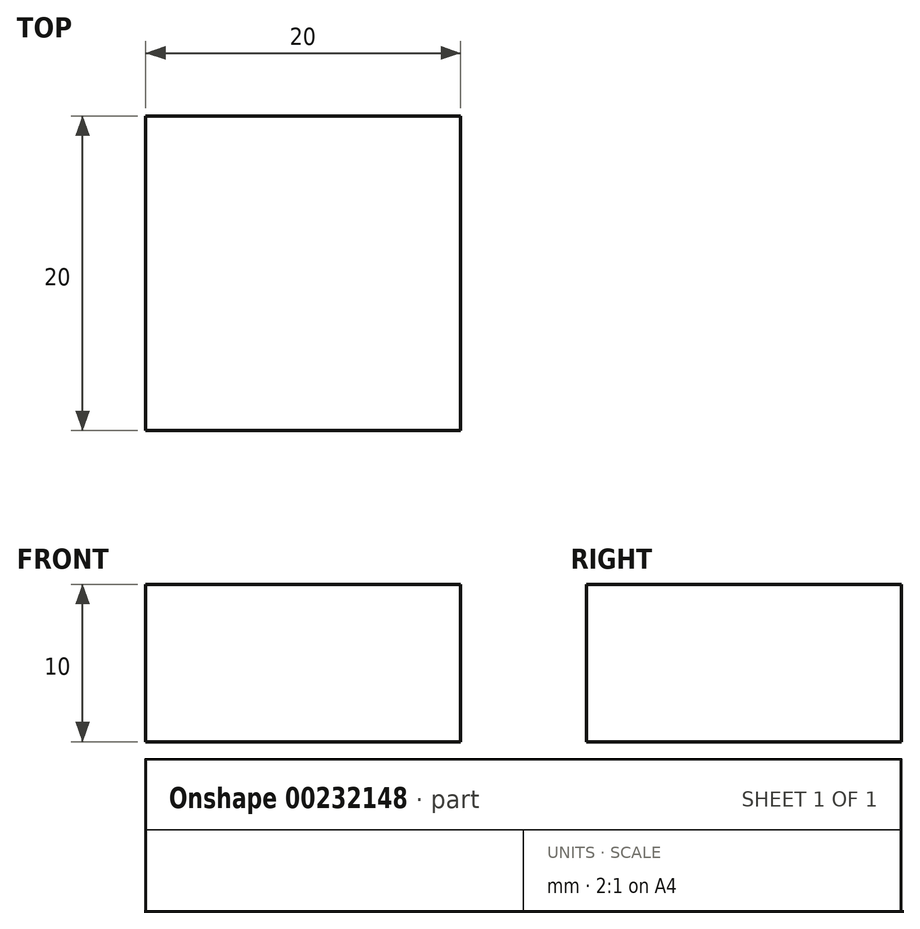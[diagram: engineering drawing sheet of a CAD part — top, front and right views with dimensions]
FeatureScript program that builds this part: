
annotation { "Feature Type Name" : "Feature", "Feature Type Description" : "" }
export const myFeature = defineFeature(function(context is Context, id is Id, definition is map)
    precondition{}
    {
        {
            var Q0;
            Q0=qCreatedBy(makeId("Top.planeOp"),FACE);
            var sketch = newSketch(context, id + "F0", { "sketchPlane" : qUnion([Q0])});
            skLineSegment(sketch, "E0.bottom", {"start": v(-10, 10) * mm, "end": v(10, 10) * mm});
            skLineSegment(sketch, "E0.top", {"start": v(-10, -10) * mm, "end": v(10, -10) * mm});
            skLineSegment(sketch, "E0.left", {"start": v(-10, 10) * mm, "end": v(-10, -10) * mm});
            skLineSegment(sketch, "E0.right", {"start": v(10, 10) * mm, "end": v(10, -10) * mm});
            skSolve(sketch);
        }
        {
            var Q0;
            Q0 = qSketchRegion(id + "F0", true);
            extrude(context, id + "F1", {"entities" : qUnion([Q0]), "depth" : 10 * mm});
        }
    });
